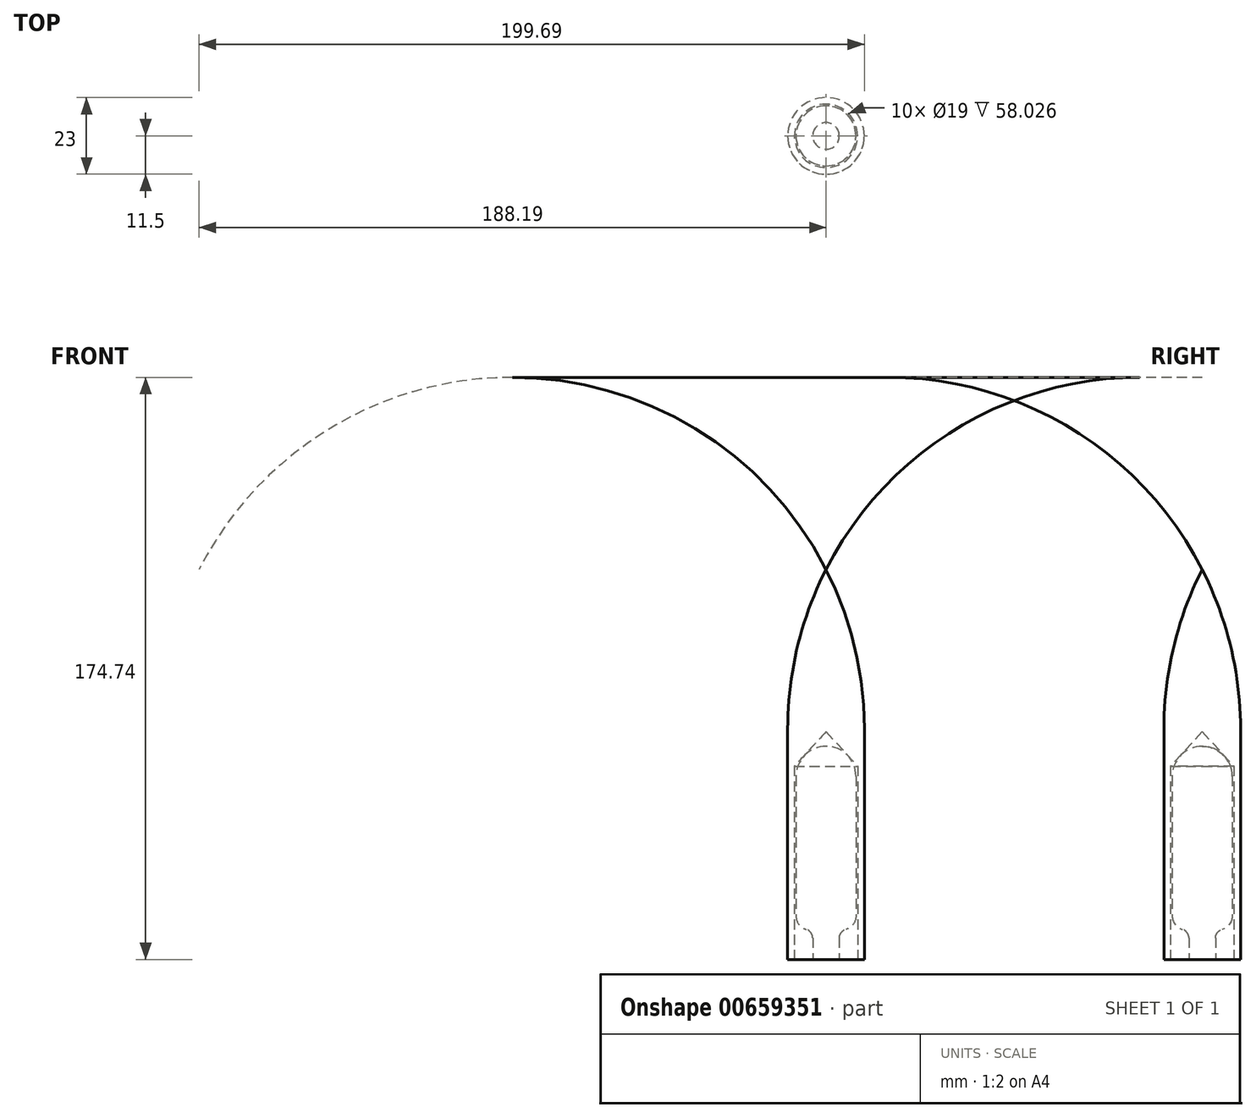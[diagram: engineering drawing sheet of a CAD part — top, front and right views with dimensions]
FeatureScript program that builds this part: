
annotation { "Feature Type Name" : "Feature", "Feature Type Description" : "" }
export const myFeature = defineFeature(function(context is Context, id is Id, definition is map)
    precondition{}
    {
        {
            var Q0;
            Q0=qCreatedBy(makeId("Right.planeOp"),FACE);
            var sketch = newSketch(context, id + "F0", { "sketchPlane" : qUnion([Q0])});
            skLineSegment(sketch, "E0", {"start": v(0, 0) * mm, "end": v(0, 64) * mm});
            skLineSegment(sketch, "E1", {"start": v(4, 0) * mm, "end": v(4, 6.45) * mm});
            skLineSegment(sketch, "E2", {"start": v(0, 0) * mm, "end": v(4, 0) * mm});
            skLineSegment(sketch, "E3", {"start": v(9, 13.1) * mm, "end": v(9, 55) * mm});
            skArc(sketch, "E4", {"start": v(9, 55) * mm, "mid": v(6.36, 61.36) * mm, "end": v(0, 64) * mm});
            skArc(sketch, "E5", {"start": v(5.94, 9.02) * mm, "mid": v(8.15, 10.55) * mm, "end": v(9, 13.1) * mm});
            skArc(sketch, "E6", {"start": v(5.94, 9.02) * mm, "mid": v(4.54, 8.06) * mm, "end": v(4, 6.45) * mm});
            skSolve(sketch);
        }
        {
            var Q0;
            Q0=makeQuery(id+"F0.imprint","IMPRINT",FACE,{"disambiguationData":[TD([[makeQuery(id+"F0.imprint","IMPRINT",EDGE,{"derivedFrom":sQuery(id+"F0.wireOp",EDGE,"E0")}),-1.0]])]});
            var Q1;
            Q1=sQuery(id+"F0.wireOp",EDGE,"E0");
            revolve(context, id + "F1", {"entities" : qUnion([Q0]), "axis" : qUnion([Q1]), "revolveType" : RevolveType.FULL});
        }
        {
            var Q0;
            Q0=qCreatedBy(makeId("Right.planeOp"),FACE);
            var sketch = newSketch(context, id + "F2", { "sketchPlane" : qUnion([Q0])});
            skLineSegment(sketch, "E7", {"start": v(0, 0) * mm, "end": v(0, 117.07) * mm});
            skLineSegment(sketch, "E8", {"start": v(11.5, 0) * mm, "end": v(11.5, 69.15) * mm});
            skLineSegment(sketch, "E9", {"start": v(9.5, 58.03) * mm, "end": v(0, 68.34) * mm});
            skArc(sketch, "E10", {"start": v(11.5, 69.15) * mm, "mid": v(8.58, 93.79) * mm, "end": v(0, 117.07) * mm});
            skLineSegment(sketch, "E11", {"start": v(11.5, 0) * mm, "end": v(9.5, 0) * mm});
            skLineSegment(sketch, "E12", {"start": v(9.5, 0) * mm, "end": v(9.5, 58.03) * mm});
            skSolve(sketch);
        }
        {
            var Q0;
            Q0=makeQuery(id+"F2.imprint","IMPRINT",FACE,{"disambiguationData":[TD([[makeQuery(id+"F2.imprint","IMPRINT",EDGE,{"derivedFrom":sQuery(id+"F2.wireOp",EDGE,"E8")}),1.0]])]});
            var Q1;
            Q1=sQuery(id+"F2.wireOp",EDGE,"E7");
            revolve(context, id + "F3", {"entities" : qUnion([Q0]), "axis" : qUnion([Q1]), "revolveType" : RevolveType.FULL});
        }
    });
